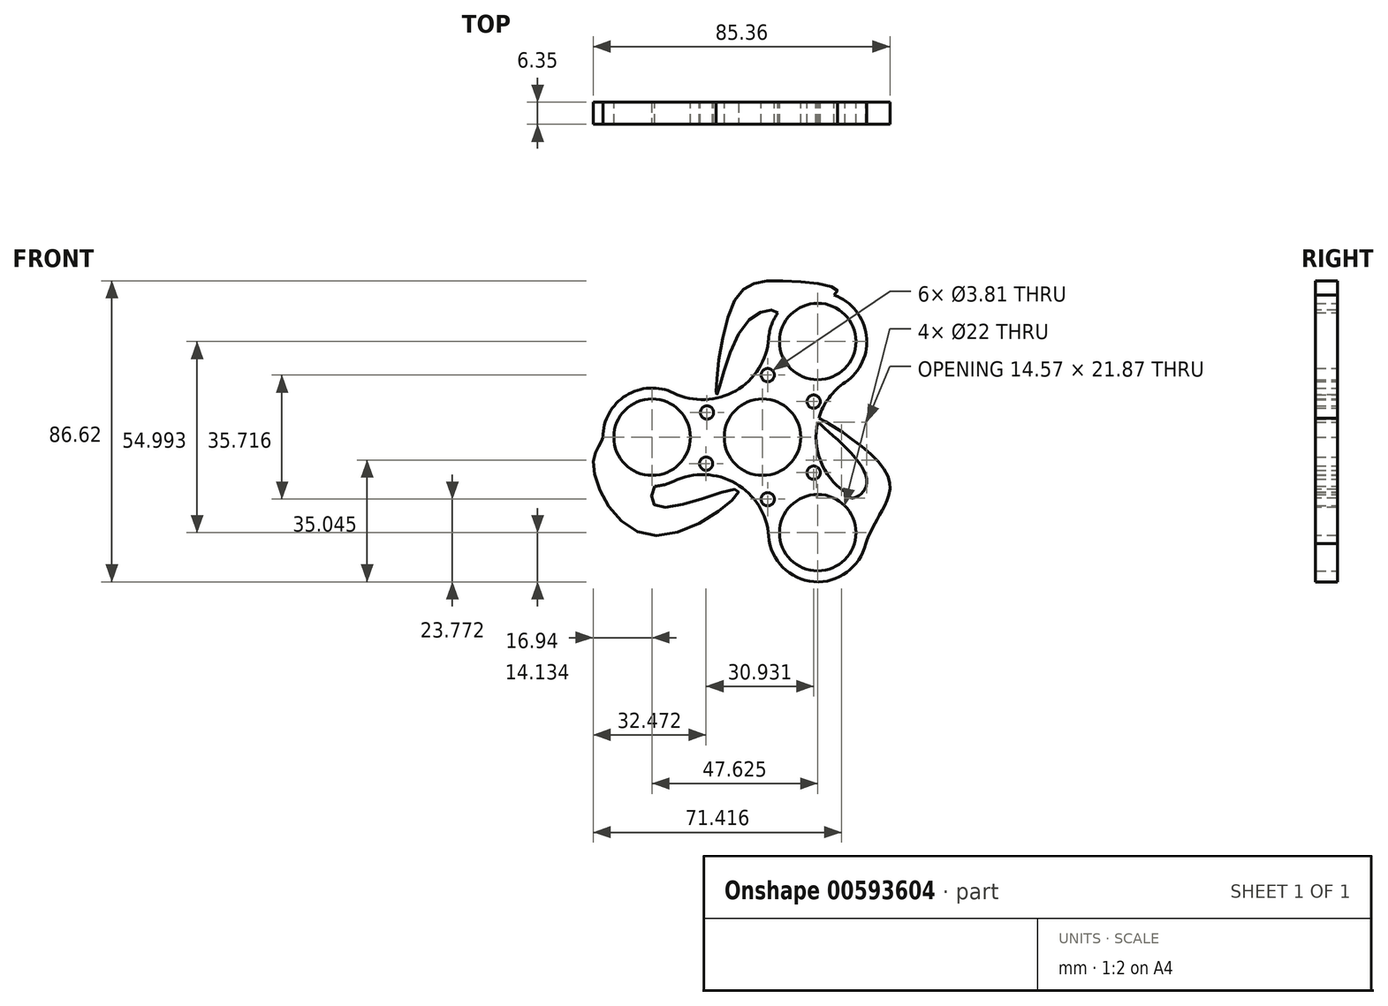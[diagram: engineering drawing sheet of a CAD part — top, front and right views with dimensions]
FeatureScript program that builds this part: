
annotation { "Feature Type Name" : "Feature", "Feature Type Description" : "" }
export const myFeature = defineFeature(function(context is Context, id is Id, definition is map)
    precondition{}
    {
        {
            var Q0;
            Q0=qCreatedBy(makeId("Front.planeOp"),FACE);
            var sketch = newSketch(context, id + "F0", { "sketchPlane" : qUnion([Q0])});
            skCircle(sketch, "E0", {"center": v(0, 0) * mm, "radius": 14.29 * mm});
            skCircle(sketch, "E1", {"center": v(0, 0) * mm, "radius": 11 * mm});
            skCircle(sketch, "E2", {"center": v(-31.75, 0) * mm, "radius": 14.13 * mm});
            skCircle(sketch, "E3", {"center": v(-31.75, 0) * mm, "radius": 11 * mm});
            skCircle(sketch, "E4.1.0", {"center": v(15.87, -27.5) * mm, "radius": 14.13 * mm});
            skCircle(sketch, "E4.1.1", {"center": v(15.87, -27.5) * mm, "radius": 11 * mm});
            skCircle(sketch, "E4.2.0", {"center": v(15.88, 27.5) * mm, "radius": 14.13 * mm});
            skCircle(sketch, "E4.2.1", {"center": v(15.88, 27.5) * mm, "radius": 11 * mm});
            skArc(sketch, "E5", {"start": v(-25.56, 12.7) * mm, "mid": v(-7.7, 13.33) * mm, "end": v(1.78, 28.49) * mm});
            skArc(sketch, "E6", {"start": v(1.78, -28.49) * mm, "mid": v(-7.7, -13.33) * mm, "end": v(-25.56, -12.7) * mm});
            skArc(sketch, "E7", {"start": v(23.78, 15.79) * mm, "mid": v(15.4, 0) * mm, "end": v(23.78, -15.79) * mm});
            skSolve(sketch);
        }
        {
            var Q0;
            Q0=makeQuery(id+"F0.imprint","IMPRINT",FACE,{"disambiguationData":[TD([[makeQuery(id+"F0.imprint","IMPRINT",EDGE,{"derivedFrom":sQuery(id+"F0.wireOp",EDGE,"E0")}),-1.0]])]});
            var sketch = newSketch(context, id + "F1", { "sketchPlane" : qUnion([Q0])});
            skCircle(sketch, "E8", {"center": v(-15.96, 7.08) * mm, "radius": 1.9 * mm});
            skCircle(sketch, "E9", {"center": v(-16.22, -7.63) * mm, "radius": 1.9 * mm});
            skCircle(sketch, "E10", {"center": v(1.5, -17.86) * mm, "radius": 1.9 * mm});
            skCircle(sketch, "E11", {"center": v(14.71, -10.23) * mm, "radius": 1.9 * mm});
            skCircle(sketch, "E12", {"center": v(14.71, 10.23) * mm, "radius": 1.9 * mm});
            skCircle(sketch, "E13", {"center": v(1.5, 17.86) * mm, "radius": 1.9 * mm});
            skArc(sketch, "E14.0.0", {"start": v(1.78, 28.49) * mm, "mid": v(-7.7, 13.33) * mm, "end": v(-25.56, 12.7) * mm});
            skArc(sketch, "E14.0.1", {"start": v(-25.56, 12.7) * mm, "mid": v(-17.62, 0) * mm, "end": v(-25.56, -12.7) * mm});
            skArc(sketch, "E14.0.2", {"start": v(-25.56, -12.7) * mm, "mid": v(-7.7, -13.33) * mm, "end": v(1.78, -28.49) * mm});
            skArc(sketch, "E14.0.3", {"start": v(1.78, -28.49) * mm, "mid": v(8.81, -15.26) * mm, "end": v(23.78, -15.79) * mm});
            skArc(sketch, "E14.0.4", {"start": v(23.78, -15.79) * mm, "mid": v(15.4, 0) * mm, "end": v(23.78, 15.79) * mm});
            skArc(sketch, "E14.0.5", {"start": v(23.78, 15.79) * mm, "mid": v(8.81, 15.26) * mm, "end": v(1.78, 28.49) * mm});
            skCircle(sketch, "E15.0", {"center": v(-31.75, 0) * mm, "radius": 11 * mm});
            skCircle(sketch, "E16.0", {"center": v(15.87, -27.5) * mm, "radius": 11 * mm});
            skCircle(sketch, "E17.0", {"center": v(15.88, 27.5) * mm, "radius": 11 * mm});
            skCircle(sketch, "E18.0", {"center": v(15.87, -27.5) * mm, "radius": 14.13 * mm});
            skCircle(sketch, "E19.0", {"center": v(-31.75, 0) * mm, "radius": 14.13 * mm});
            skCircle(sketch, "E20.0", {"center": v(0, 0) * mm, "radius": 14.29 * mm});
            skCircle(sketch, "E21.0", {"center": v(0, 0) * mm, "radius": 11 * mm});
            skSolve(sketch);
        }
        {
            var Q0;
            Q0=makeQuery(id+"F0.imprint","IMPRINT",FACE,{"disambiguationData":[TD([[makeQuery(id+"F0.imprint","IMPRINT",EDGE,{"derivedFrom":sQuery(id+"F0.wireOp",EDGE,"E3")}),-1.0]])]});
            var sketch = newSketch(context, id + "F2", { "sketchPlane" : qUnion([Q0])});
            skFitSpline(sketch, "E22", {"points": [v(-25.4, -12.62) * mm, v(-29.5, -13.95) * mm, v(-28.91, -17.29) * mm, v(-15.46, -18.06) * mm, v(-28.33, -22.48) * mm, v(-46.4, -7.3) * mm, v(-45.88, 0) * mm], "startDerivative": vector(-43.47, -6.38) * mm, "endDerivative": vector(18.02, 43.74) * mm});
            skFitSpline(sketch, "E23", {"points": [v(1.77, 28.24) * mm, v(-2, 32.08) * mm, v(-10.83, 20.36) * mm, v(-7.18, 34.58) * mm, v(7.6, 43.22) * mm, v(19.88, 41.04) * mm, v(19.33, 40.53) * mm, v(19.4, 41.18) * mm], "startDerivative": vector(67.25, 188.46) * mm, "endDerivative": vector(4.4, 16.81) * mm});
            skFitSpline(sketch, "E24", {"points": [v(23.74, -15.76) * mm, v(27, -12.5) * mm, v(20.85, 0) * mm, v(32, -9.42) * mm, v(33.72, -20.37) * mm, v(28.21, -34.38) * mm], "startDerivative": vector(50.94, -41.58) * mm, "endDerivative": vector(-34.5, -85.85) * mm});
            skFitSpline(sketch, "E25", {"points": [v(23.74, -15.76) * mm, v(26.23, -17.85) * mm, v(28.3, -20.6) * mm, v(29.74, -24.8) * mm, v(29.9, -29.19) * mm, v(28.21, -34.38) * mm], "startDerivative": vector(15.47, -11.7) * mm, "endDerivative": vector(-10.84, -22.18) * mm});
            skFitSpline(sketch, "E26", {"points": [v(1.77, 28.24) * mm, v(2.23, 31.3) * mm, v(3.56, 34.32) * mm, v(6.27, 37.85) * mm, v(10.64, 40.62) * mm, v(15.73, 41.63) * mm, v(19.88, 41.04) * mm, v(19.4, 41.18) * mm], "startDerivative": vector(2.12, 22.92) * mm, "endDerivative": vector(-13.85, 3.62) * mm});
            skCircle(sketch, "E27.0", {"center": v(-15.96, 7.08) * mm, "radius": 1.9 * mm});
            skCircle(sketch, "E27.1", {"center": v(1.5, 17.86) * mm, "radius": 1.9 * mm});
            skCircle(sketch, "E27.2", {"center": v(14.71, 10.23) * mm, "radius": 1.9 * mm});
            skCircle(sketch, "E27.3", {"center": v(14.71, -10.23) * mm, "radius": 1.9 * mm});
            skCircle(sketch, "E27.4", {"center": v(1.5, -17.86) * mm, "radius": 1.9 * mm});
            skCircle(sketch, "E27.5", {"center": v(-16.22, -7.63) * mm, "radius": 1.9 * mm});
            skArc(sketch, "E28.0", {"start": v(-25.56, 12.7) * mm, "mid": v(-7.7, 13.33) * mm, "end": v(1.78, 28.49) * mm});
            skCircle(sketch, "E29.0", {"center": v(-31.75, 0) * mm, "radius": 14.13 * mm});
            skCircle(sketch, "E30.0", {"center": v(-31.75, 0) * mm, "radius": 11 * mm});
            skArc(sketch, "E31.0", {"start": v(1.78, -28.49) * mm, "mid": v(-7.7, -13.33) * mm, "end": v(-25.56, -12.7) * mm});
            skCircle(sketch, "E32.0", {"center": v(15.87, -27.5) * mm, "radius": 14.13 * mm});
            skCircle(sketch, "E33.0", {"center": v(15.87, -27.5) * mm, "radius": 11 * mm});
            skCircle(sketch, "E34.0", {"center": v(0, 0) * mm, "radius": 14.29 * mm});
            skCircle(sketch, "E35.0", {"center": v(0, 0) * mm, "radius": 11 * mm});
            skArc(sketch, "E36.0", {"start": v(23.78, 15.79) * mm, "mid": v(15.4, 0) * mm, "end": v(23.78, -15.79) * mm});
            skCircle(sketch, "E37.0", {"center": v(15.88, 27.5) * mm, "radius": 14.13 * mm});
            skCircle(sketch, "E38.0", {"center": v(15.88, 27.5) * mm, "radius": 11 * mm});
            skArc(sketch, "E39.0.0", {"start": v(1.78, 28.49) * mm, "mid": v(-7.7, 13.33) * mm, "end": v(-25.56, 12.7) * mm});
            skArc(sketch, "E39.0.1", {"start": v(-25.56, 12.7) * mm, "mid": v(-17.62, 0) * mm, "end": v(-25.56, -12.7) * mm});
            skArc(sketch, "E39.0.2", {"start": v(-25.56, -12.7) * mm, "mid": v(-7.7, -13.33) * mm, "end": v(1.78, -28.49) * mm});
            skArc(sketch, "E39.0.3", {"start": v(1.78, -28.49) * mm, "mid": v(8.81, -15.26) * mm, "end": v(23.78, -15.79) * mm});
            skArc(sketch, "E39.0.4", {"start": v(23.78, -15.79) * mm, "mid": v(15.4, 0) * mm, "end": v(23.78, 15.79) * mm});
            skArc(sketch, "E39.0.5", {"start": v(23.78, 15.79) * mm, "mid": v(8.81, 15.26) * mm, "end": v(1.78, 28.49) * mm});
            skArc(sketch, "E40.0.0", {"start": v(-25.56, -12.7) * mm, "mid": v(-17.62, 0) * mm, "end": v(-25.56, 12.7) * mm});
            skArc(sketch, "E40.0.1", {"start": v(-25.56, 12.7) * mm, "mid": v(-45.88, 0) * mm, "end": v(-25.56, -12.7) * mm});
            skArc(sketch, "E41.0.0", {"start": v(1.78, 28.49) * mm, "mid": v(8.81, 15.26) * mm, "end": v(23.78, 15.79) * mm});
            skArc(sketch, "E41.0.1", {"start": v(23.78, 15.79) * mm, "mid": v(22.94, 39.73) * mm, "end": v(1.78, 28.49) * mm});
            skArc(sketch, "E42.0.0", {"start": v(23.78, -15.79) * mm, "mid": v(8.81, -15.26) * mm, "end": v(1.78, -28.49) * mm});
            skArc(sketch, "E42.0.1", {"start": v(1.78, -28.49) * mm, "mid": v(22.94, -39.73) * mm, "end": v(23.78, -15.79) * mm});
            skSolve(sketch);
        }
        {
            var Q0;
            Q0=qCreatedBy(makeId("Front.planeOp"),FACE);
            var sketch = newSketch(context, id + "F3", { "sketchPlane" : qUnion([Q0])});
            skCircle(sketch, "E43.0", {"center": v(-15.96, 7.08) * mm, "radius": 1.9 * mm});
            skCircle(sketch, "E44.0", {"center": v(1.5, 17.86) * mm, "radius": 1.9 * mm});
            skCircle(sketch, "E45.0", {"center": v(14.71, 10.23) * mm, "radius": 1.9 * mm});
            skCircle(sketch, "E46.0", {"center": v(14.71, -10.23) * mm, "radius": 1.9 * mm});
            skCircle(sketch, "E47.0", {"center": v(1.5, -17.86) * mm, "radius": 1.9 * mm});
            skCircle(sketch, "E48.0", {"center": v(-16.22, -7.63) * mm, "radius": 1.9 * mm});
            skCircle(sketch, "E49.0", {"center": v(-31.75, 0) * mm, "radius": 11 * mm});
            skArc(sketch, "E50.0", {"start": v(-25.56, -12.7) * mm, "mid": v(-17.62, 0) * mm, "end": v(-25.56, 12.7) * mm});
            skFitSpline(sketch, "E51.0", {"points": [v(1.77, 28.24) * mm, v(4.45, 35.78) * mm, v(-4.9, 32.66) * mm, v(-13.16, 12.21) * mm, v(-8.57, 38.24) * mm, v(5.32, 44.98) * mm, v(21.57, 41.9) * mm, v(19.07, 40.2) * mm, v(19.33, 40.95) * mm, v(19.4, 41.18) * mm]});
            skFitSpline(sketch, "E52.0", {"points": [v(-25.4, -12.62) * mm, v(-26.99, -12.85) * mm, v(-30.1, -13) * mm, v(-30.67, -19.79) * mm, v(-7.08, -15.15) * mm, v(-31.37, -28.34) * mm, v(-48.68, -7.97) * mm, v(-46.74, -2.1) * mm, v(-45.88, 0) * mm]});
            skPoint(sketch, "E53.0", {"position": v(-7.7, -13.33) * mm});
            skCircle(sketch, "E54.0", {"center": v(0, 0) * mm, "radius": 14.29 * mm});
            skArc(sketch, "E55.0", {"start": v(-25.56, -12.7) * mm, "mid": v(-7.7, -13.33) * mm, "end": v(1.78, -28.49) * mm});
            skCircle(sketch, "E56.0", {"center": v(15.87, -27.5) * mm, "radius": 14.13 * mm});
            skCircle(sketch, "E57.0", {"center": v(15.87, -27.5) * mm, "radius": 11 * mm});
            skFitSpline(sketch, "E58.0", {"points": [v(23.74, -15.76) * mm, v(25.9, -17.52) * mm, v(29.87, -11.5) * mm, v(14.17, 6.18) * mm, v(35.14, -9.5) * mm, v(34.3, -21.16) * mm, v(30.85, -27.81) * mm, v(28.21, -34.38) * mm]});
            skArc(sketch, "E59.0", {"start": v(23.78, -15.79) * mm, "mid": v(15.4, 0) * mm, "end": v(23.78, 15.79) * mm});
            skCircle(sketch, "E60.0", {"center": v(15.88, 27.5) * mm, "radius": 14.13 * mm});
            skArc(sketch, "E61.0", {"start": v(-25.56, 12.7) * mm, "mid": v(-7.7, 13.33) * mm, "end": v(1.78, 28.49) * mm});
            skCircle(sketch, "E62.0", {"center": v(15.88, 27.5) * mm, "radius": 11 * mm});
            skArc(sketch, "E63.0", {"start": v(-25.56, 12.7) * mm, "mid": v(-45.88, 0) * mm, "end": v(-25.56, -12.7) * mm});
            skCircle(sketch, "E64.0", {"center": v(0, 0) * mm, "radius": 11 * mm});
            skSolve(sketch);
        }
        {
            var Q0;
            Q0 = qSketchRegion(id + "F3", true);
            extrude(context, id + "F4", {"entities" : qUnion([Q0]), "depth" : 6.35 * mm, "offsetDistance" : 25.4 * mm});
        }
        {
            var Q0;
            Q0=qCreatedBy(makeId("Front.planeOp"),FACE);
            var sketch = newSketch(context, id + "F5", { "sketchPlane" : qUnion([Q0])});
            skCircle(sketch, "E65.0", {"center": v(0, 0) * mm, "radius": 11 * mm});
            skCircle(sketch, "E66.0", {"center": v(0, 0) * mm, "radius": 14.29 * mm});
            skSolve(sketch);
        }
        {
            var Q0;
            Q0 = qSketchRegion(id + "F5", true);
            extrude(context, id + "F6", {"entities" : qUnion([Q0]), "operationType" : NewBodyOperationType.ADD, "depth" : 6.35 * mm, "offsetDistance" : 25.4 * mm});
        }
    });
